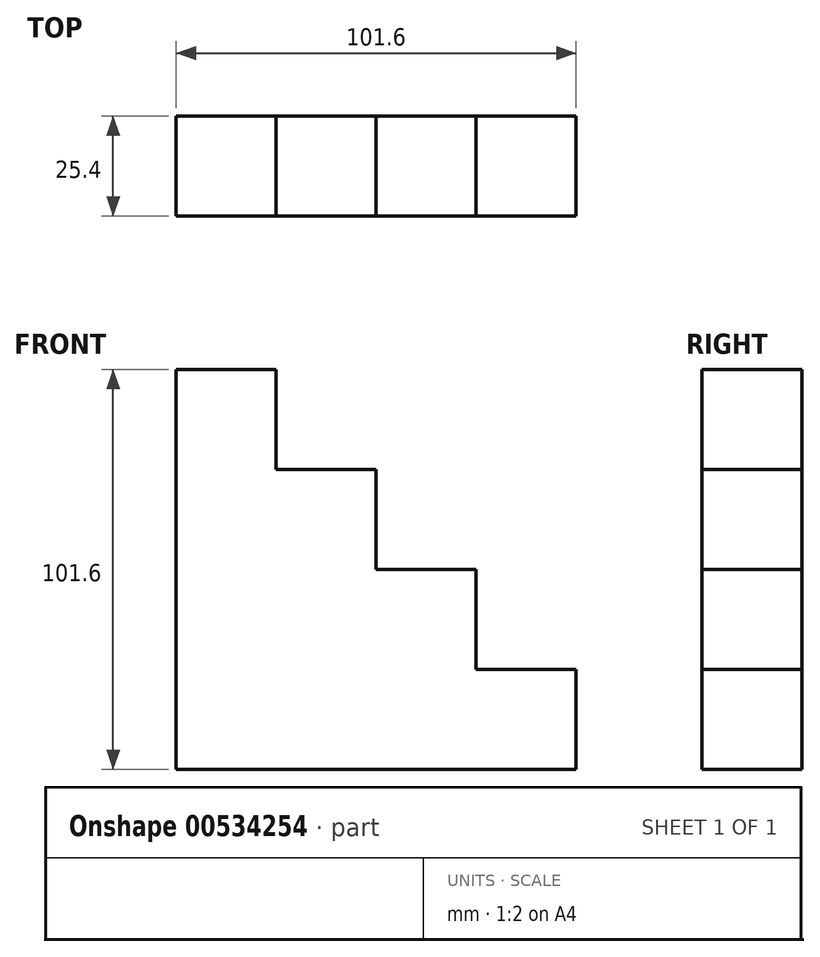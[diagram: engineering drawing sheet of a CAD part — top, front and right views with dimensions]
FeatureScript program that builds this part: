
annotation { "Feature Type Name" : "Feature", "Feature Type Description" : "" }
export const myFeature = defineFeature(function(context is Context, id is Id, definition is map)
    precondition{}
    {
        {
            var Q0;
            Q0=qCreatedBy(makeId("Front.planeOp"),FACE);
            var sketch = newSketch(context, id + "F0", { "sketchPlane" : qUnion([Q0])});
            skLineSegment(sketch, "E0", {"start": v(-76.38, 32.98) * mm, "end": v(-50.98, 32.98) * mm});
            skLineSegment(sketch, "E1", {"start": v(-50.98, 32.98) * mm, "end": v(-50.98, 7.58) * mm});
            skLineSegment(sketch, "E2", {"start": v(-50.98, 7.58) * mm, "end": v(-25.58, 7.58) * mm});
            skLineSegment(sketch, "E3", {"start": v(-25.58, 7.58) * mm, "end": v(-25.58, -17.82) * mm});
            skLineSegment(sketch, "E4", {"start": v(-25.58, -17.82) * mm, "end": v(-0.18, -17.82) * mm});
            skLineSegment(sketch, "E5", {"start": v(-0.18, -17.82) * mm, "end": v(-0.18, -43.22) * mm});
            skLineSegment(sketch, "E6", {"start": v(-0.18, -43.22) * mm, "end": v(25.22, -43.22) * mm});
            skLineSegment(sketch, "E7", {"start": v(25.22, -43.22) * mm, "end": v(25.22, -68.62) * mm});
            skLineSegment(sketch, "E8", {"start": v(-76.38, 32.98) * mm, "end": v(-76.38, -68.62) * mm});
            skLineSegment(sketch, "E9", {"start": v(-76.38, -68.62) * mm, "end": v(25.22, -68.62) * mm});
            skSolve(sketch);
        }
        {
            var Q0;
            Q0 = qSketchRegion(id + "F0", true);
            extrude(context, id + "F1", {"entities" : qUnion([Q0]), "depth" : 25.4 * mm, "offsetDistance" : 25.4 * mm});
        }
    });
